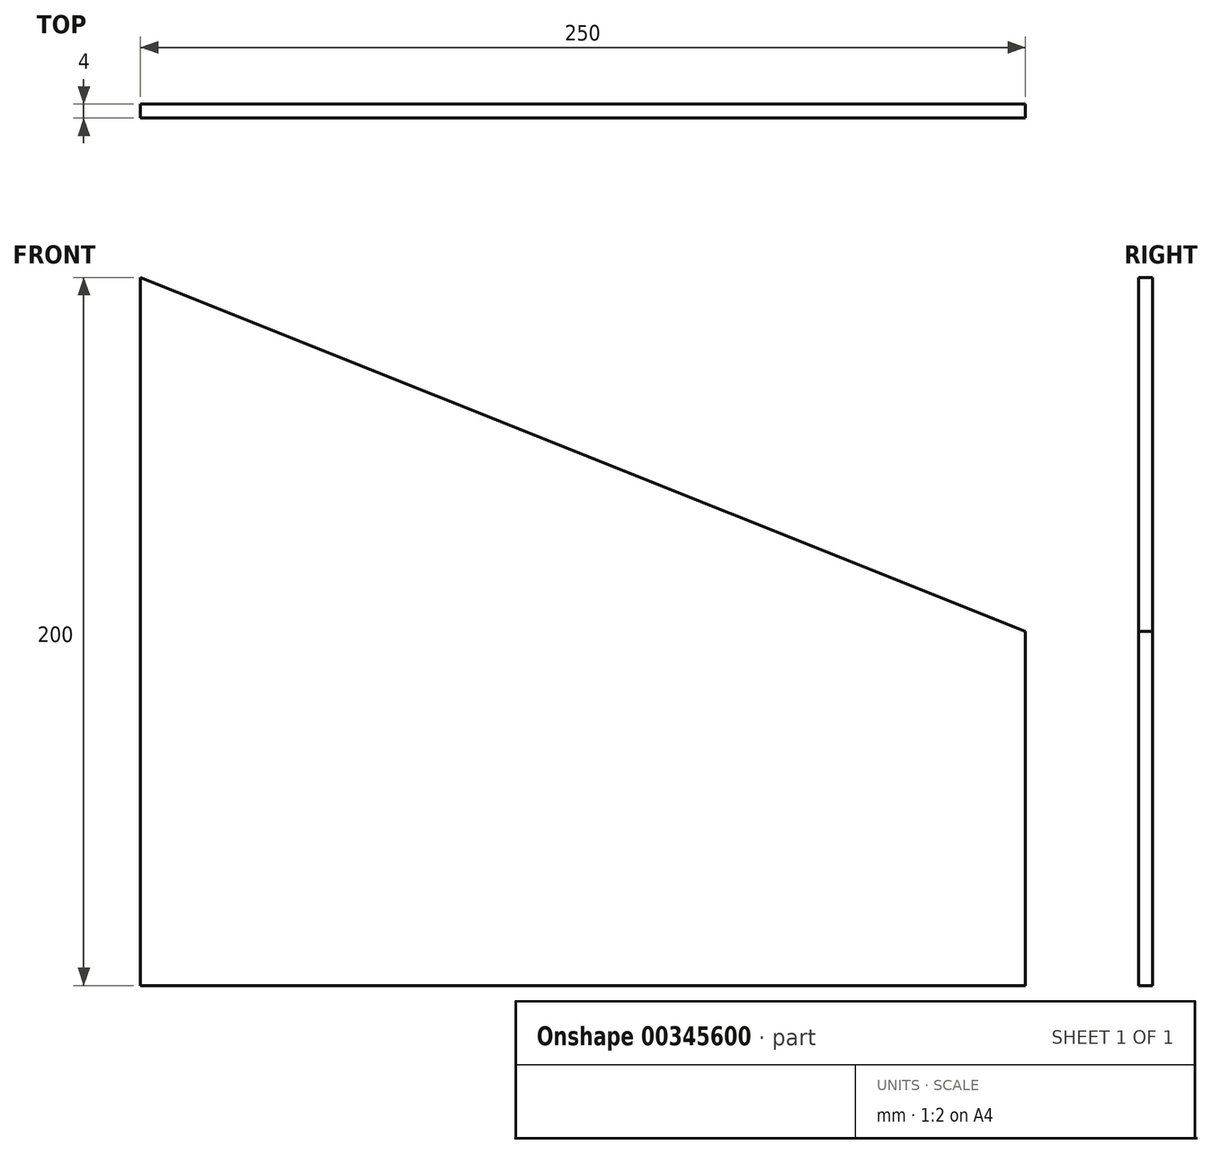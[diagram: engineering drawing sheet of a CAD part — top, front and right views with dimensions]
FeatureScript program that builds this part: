
annotation { "Feature Type Name" : "Feature", "Feature Type Description" : "" }
export const myFeature = defineFeature(function(context is Context, id is Id, definition is map)
    precondition{}
    {
        {
            var Q0;
            Q0=qCreatedBy(makeId("Front.planeOp"),FACE);
            var sketch = newSketch(context, id + "F0", { "sketchPlane" : qUnion([Q0])});
            skLineSegment(sketch, "E0", {"start": v(0, 0) * mm, "end": v(0, 200) * mm});
            skLineSegment(sketch, "E1", {"start": v(0, 200) * mm, "end": v(250, 100) * mm});
            skLineSegment(sketch, "E2", {"start": v(250, 100) * mm, "end": v(250, 0) * mm});
            skLineSegment(sketch, "E3", {"start": v(250, 0) * mm, "end": v(0, 0) * mm});
            skSolve(sketch);
        }
        {
            var Q0;
            Q0 = qSketchRegion(id + "F0", true);
            extrude(context, id + "F1", {"entities" : qUnion([Q0]), "depth" : 4 * mm});
        }
    });
